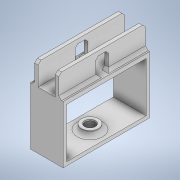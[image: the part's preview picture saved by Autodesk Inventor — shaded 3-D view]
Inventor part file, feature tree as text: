
AUTODESK INVENTOR PART (.ipt)
format: ipt  version: 2020 (Build 240168000, 168)  size: 243,200 bytes
history: native  units: mm
features: extrude x8, sketch x8, chamfer x2, fillet x1
ambient origin geometry x8: Origin, YZ Plane, XZ Plane, XY Plane, X Axis, Y Axis, Z Axis, Center Point
bodies: Solid1 (feature_tree)
feature tree (19):
  extrude  "Extrusion1"  Depth=61.0mm
  extrude  "Extrusion2"  TaperAngle=0.0deg  [1 undecoded]
  extrude  "Extrusion3"  Depth=2.5mm
  extrude  "Extrusion4"  Depth=6.0mm
  extrude  "Extrusion5"  Depth=56.0mm
  extrude  "Extrusion6"  Depth=3.0mm
  extrude  "Extrusion7"  Depth=3.0mm TaperAngle=0.0deg
  chamfer  "Chamfer1"  [1 undecoded]
  chamfer  "Chamfer2"  Distance=2.5mm
  fillet  "Fillet1"  Radius=2.5mm
  extrude  "Extrusion8"  Depth=35.0mm TaperAngle=0.0deg
  sketch  "Sketch1"  dims[d0=61.0mm d1=30.5mm]
  sketch  "Sketch2"  dims[d2=0.0mm d3=0.0mm]
  sketch  "Sketch3"  dims[d4=2.5mm d5=2.5mm]
  sketch  "Sketch4"  dims[d6=12.0mm d7=6.0mm]
  sketch  "Sketch5"  dims[d8=15.5mm d9=0.0mm d10=56.0mm]
  sketch  "Sketch6"  dims[d11=28.0mm d12=3.0mm]
  sketch  "Sketch7"  dims[d13=3.0mm d14=3.0mm d15=0.0mm]
  sketch  "Sketch8"  dims[d16=0.0mm d17=0.0mm d18=2.5mm d19=2.5mm d20=35.0mm d21=3.0mm d22=0.0mm d23=0.0mm d24=2.5mm d25=0.0mm d26=12.0mm d27=3.0mm d28=6.0mm d29=0.0mm d30=0.0mm d31=7.5mm d32=10.0mm d33=8.0mm d34=0.0mm d35=0.0mm d36=9.0mm d37=4.5mm d38=12.5mm d39=0.0mm d40=2.0mm d41=2.0mm d42=45.0deg d43=2.0mm d44=2.0mm d45=45.0deg d46=3.0mm d47=10.0mm d48=0.0mm]
note: 2 required parameter values undecoded (feature->parameter linkage not recoverable at this tier; creation-order binding heuristic only, values carry confidence <= 0.55)
